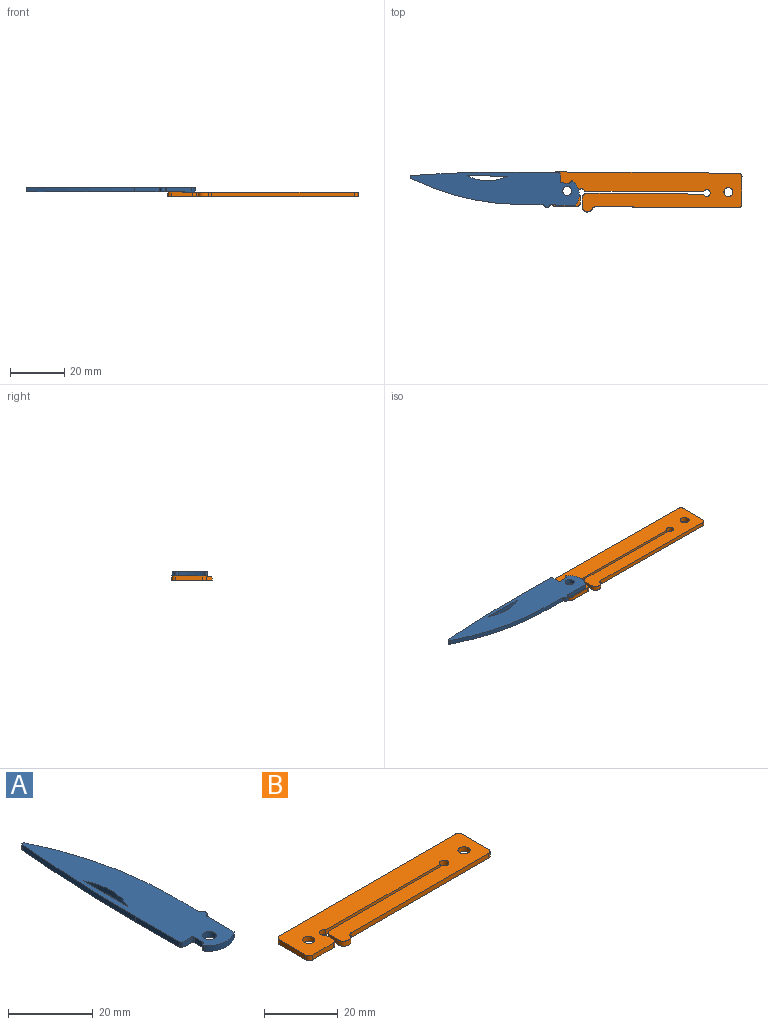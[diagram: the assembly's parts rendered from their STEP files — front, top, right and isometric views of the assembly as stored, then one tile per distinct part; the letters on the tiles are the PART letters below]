
ASSEMBLY  parts=2 mates=1
PART A: 21 faces, bbox 13x62.4x1.6 mm
  f0: plane 8.98x1.59mm, normal (1,0,0), area 14.3mm2, adj f1,f9,f10,f17
  f1: cylinder r=90.99mm len=39.8mm, axis (0,0,-1), area 65.4mm2, adj f0,f9,f10,f12
  f2: cylinder r=435.3mm len=39.63mm, axis (0,0,-1), area 63mm2, adj f3,f9,f10,f12
  f3: plane 14.68x1.59mm, normal (-1,0,0), area 23.3mm2, adj f2,f9,f10,f13
  f4: plane 2.79x1.59mm, normal (0,-1,0), area 4.4mm2, adj f9,f10,f13,f14
  f5: plane 2.81x1.59mm, normal (-1,0,0), area 4.5mm2, adj f9,f10,f14,f18
  f6: cylinder r=6.08mm len=8.9mm, axis (0,0,-1), area 16mm2, adj f7,f9,f10,f15
  f7: plane 8.93x1.59mm, normal (1,0,0), area 14.2mm2, adj f6,f9,f10,f16
  f8: cylinder r=1.02mm len=1.92mm, axis (0,0,-1), area 4mm2, adj f9,f10,f16,f17
  f9: plane 62.37x12.95mm, normal (0,0,1), area 543.6mm2, adj f0,f1,f2,f3,f4,f5,f6,f7
  f10: plane 62.37x12.95mm, normal (0,0,-1), area 543.6mm2, adj f0,f1,f2,f3,f4,f5,f6,f7
  f11: cylinder r=1.65mm len=3.3mm, axis (0,0,1), area 16.5mm2, adj f9,f10
  f12: cylinder r=0.51mm len=1.59mm, axis (0,0,-1), area 2.1mm2, adj f1,f2,f9,f10
  f13: cylinder r=0.51mm len=1.59mm, axis (0,0,1), area 1.3mm2, adj f3,f4,f9,f10
  f14: cylinder r=0.51mm len=1.59mm, axis (0,0,1), area 1.3mm2, adj f4,f5,f9,f10
  f15: cylinder r=0.51mm len=1.59mm, axis (0,0,-1), area 1.7mm2, adj f6,f9,f10,f18
  f16: cylinder r=0.51mm len=1.59mm, axis (0,0,-1), area 1mm2, adj f7,f8,f9,f10
  f17: cylinder r=0.51mm len=1.59mm, axis (0,0,-1), area 1mm2, adj f0,f8,f9,f10
  f18: cylinder r=0.51mm len=1.59mm, axis (0,0,-1), area 1.1mm2, adj f5,f9,f10,f15
  f19: cylinder r=16.15mm len=14.73mm, axis (0,0,1), area 24.3mm2, adj f9,f10,f20
  f20: plane 14.73x1.59mm, normal (1,0,0), area 23.4mm2, adj f9,f10,f19
PART B: 23 faces, bbox 70.1x15x27 mm
  f0: plane 52.55x1.59mm, normal (0,-1,0), area 83.4mm2, adj f1,f2,f14,f18
  f1: plane 69.87x14.62mm, normal (0,0,1), area 826.2mm2, adj f0,f3,f4,f5,f6,f7,f8,f9
  f2: plane 69.87x14.71mm, normal (0,0,-1), area 826.8mm2, adj f0,f3,f4,f5,f6,f7,f8,f9
  f3: plane 67.31x1.59mm, normal (0,1,0), area 106.9mm2, adj f1,f2,f16,f19
  f4: plane 10.16x1.59mm, normal (-1,0,0), area 16.1mm2, adj f1,f2,f16,f17
  f5: plane 7.88x1.59mm, normal (0,-1,0), area 12.5mm2, adj f1,f2,f15,f17
  f6: plane 10.16x1.59mm, normal (1,0,0), area 16.1mm2, adj f1,f2,f18,f19
  f7: cylinder r=1.65mm len=3.3mm, axis (0,0,1), area 16.5mm2, adj f1,f2
  f8: cylinder r=1.65mm len=3.3mm, axis (0,0,1), area 16.5mm2, adj f1,f2
  f9: plane 2.82x1.59mm, normal (1,0,0), area 4.5mm2, adj f1,f2,f15,f21
  f10: plane 4.31x1.86mm, normal (-1,0,0), area 5.8mm2, adj f1,f2,f13,f22
  f11: plane 43.61x1.59mm, normal (0,1,0), area 69.2mm2, adj f1,f2,f20,f22
  f12: plane 43.64x1.59mm, normal (0,-1,0), area 69.3mm2, adj f1,f2,f20,f21
  f13: cone r=1.91mm half-angle=3deg, axis (0,0,-1), area 8.9mm2, adj f1,f2,f10,f14
  f14: bspline ~26.74x2.64mm, area 2.4mm2, adj f0,f1,f2,f13
  f15: cylinder r=1.27mm len=1.59mm, axis (0,0,-1), area 3.2mm2, adj f1,f2,f5,f9
  f16: cylinder r=1.27mm len=1.59mm, axis (0,0,1), area 3.2mm2, adj f1,f2,f3,f4
  f17: cylinder r=1.27mm len=1.59mm, axis (0,0,-1), area 3.2mm2, adj f1,f2,f4,f5
  f18: cylinder r=1.27mm len=1.59mm, axis (0,0,1), area 3.2mm2, adj f0,f1,f2,f6
  f19: cylinder r=1.27mm len=1.59mm, axis (0,0,-1), area 3.2mm2, adj f1,f2,f3,f6
  f20: cylinder r=1.27mm len=2.54mm, axis (0,0,1), area 11.4mm2, adj f1,f2,f11,f12
  f21: cylinder r=1.27mm len=2.46mm, axis (0,0,1), area 8mm2, adj f1,f2,f9,f12
  f22: cylinder r=1.27mm len=1.59mm, axis (0,0,1), area 2.1mm2, adj f1,f2,f10,f11
PLACE A rot(axis=(0.7,-0.71,0),180deg) t=(-72.34,-30.98,-22.69)mm
PLACE B rot(axis=(0,0,-1),0.4deg) t=(-18.77,-31.46,-25.86)mm
MATE revolute B.f8 <-> A.f11  axis (0,0,1) through (-13.27,-38.48,-24.28)mm
